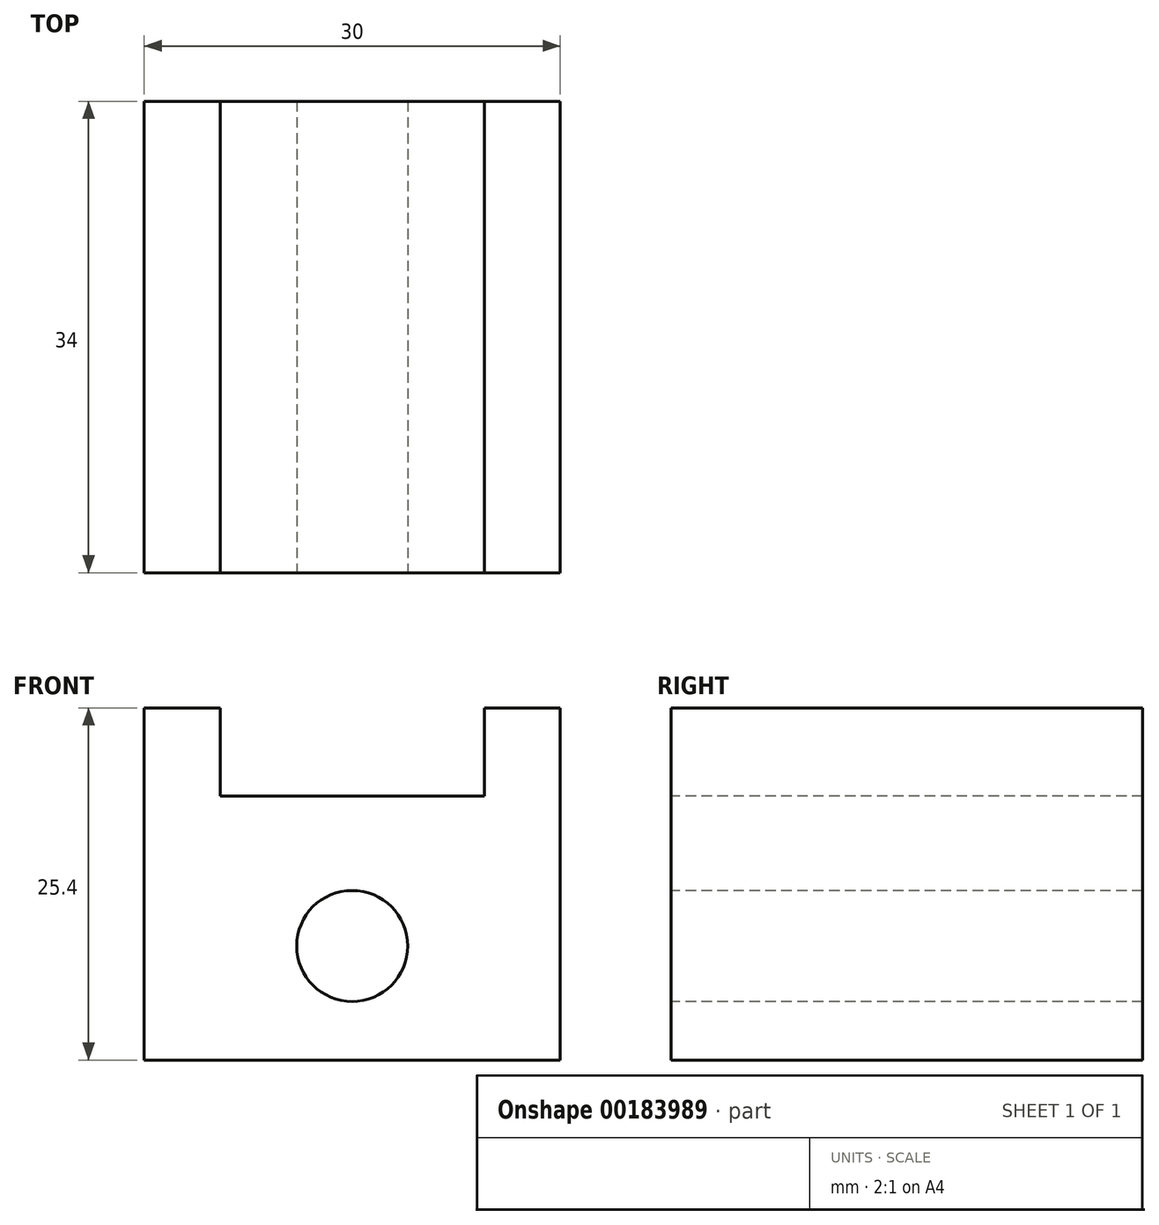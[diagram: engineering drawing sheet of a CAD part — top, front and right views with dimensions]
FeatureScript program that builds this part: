
annotation { "Feature Type Name" : "Feature", "Feature Type Description" : "" }
export const myFeature = defineFeature(function(context is Context, id is Id, definition is map)
    precondition{}
    {
        {
            var Q0;
            Q0=qCreatedBy(makeId("Top.planeOp"),FACE);
            var sketch = newSketch(context, id + "F0", { "sketchPlane" : qUnion([Q0])});
            skLineSegment(sketch, "E0.bottom", {"start": v(15, 17) * mm, "end": v(-15, 17) * mm});
            skLineSegment(sketch, "E0.top", {"start": v(15, -17) * mm, "end": v(-15, -17) * mm});
            skLineSegment(sketch, "E0.left", {"start": v(15, 17) * mm, "end": v(15, -17) * mm});
            skLineSegment(sketch, "E0.right", {"start": v(-15, 17) * mm, "end": v(-15, -17) * mm});
            skPoint(sketch, "E0.middle", {"position": v(0, 0) * mm});
            skSolve(sketch);
        }
        {
            var Q0;
            Q0=makeQuery(id+"F0.imprint","IMPRINT",FACE,{"disambiguationData":[TD([[makeQuery(id+"F0.imprint","IMPRINT",EDGE,{"derivedFrom":sQuery(id+"F0.wireOp",EDGE,"E0.bottom")}),1.0]])]});
            extrude(context, id + "F1", {"entities" : qUnion([Q0]), "depth" : 25.4 * mm});
        }
        {
            var Q0;
            Q0=makeQuery(id+"F1.opExtrude","SWEPT_FACE",FACE,{"disambiguationData":[OSD([sQuery(id+"F0.wireOp",EDGE,"E0.top")])]});
            var sketch = newSketch(context, id + "F2", { "sketchPlane" : qUnion([Q0])});
            skCircle(sketch, "E1", {"center": v(0, 8.22) * mm, "radius": 4 * mm});
            skSolve(sketch);
        }
        {
            var Q0;
            Q0=makeQuery(id+"F2.imprint","IMPRINT",FACE,{"disambiguationData":[TD([[makeQuery(id+"F2.imprint","IMPRINT",EDGE,{"derivedFrom":sQuery(id+"F2.wireOp",EDGE,"E1")}),1.0]])]});
            extrude(context, id + "F3", {"entities" : qUnion([Q0]), "operationType" : NewBodyOperationType.REMOVE, "endBound" : BoundingType.THROUGH_ALL, "oppositeDirection" : true, "depth" : 25.4 * mm});
        }
        {
            var Q0;
            Q0=makeQuery(id+"F1.opExtrude","CAP_FACE",FACE,{"disambiguationData":[OSD([sQuery(id+"F0.wireOp",EDGE,"E0.bottom"),sQuery(id+"F0.wireOp",EDGE,"E0.top"),sQuery(id+"F0.wireOp",EDGE,"E0.left"),sQuery(id+"F0.wireOp",EDGE,"E0.right")])],"isStart":false});
            var sketch = newSketch(context, id + "F4", { "sketchPlane" : qUnion([Q0])});
            skLineSegment(sketch, "E2.bottom", {"start": v(9.53, 17) * mm, "end": v(-9.53, 17) * mm});
            skLineSegment(sketch, "E2.top", {"start": v(9.53, -17) * mm, "end": v(-9.53, -17) * mm});
            skLineSegment(sketch, "E2.left", {"start": v(9.53, 17) * mm, "end": v(9.53, -17) * mm});
            skLineSegment(sketch, "E2.right", {"start": v(-9.53, 17) * mm, "end": v(-9.53, -17) * mm});
            skPoint(sketch, "E2.middle", {"position": v(0, 0) * mm});
            skSolve(sketch);
        }
        {
            var Q0;
            Q0 = qSketchRegion(id + "F4", true);
            extrude(context, id + "F5", {"entities" : qUnion([Q0]), "operationType" : NewBodyOperationType.REMOVE, "oppositeDirection" : true, "depth" : 6.35 * mm});
        }
    });
